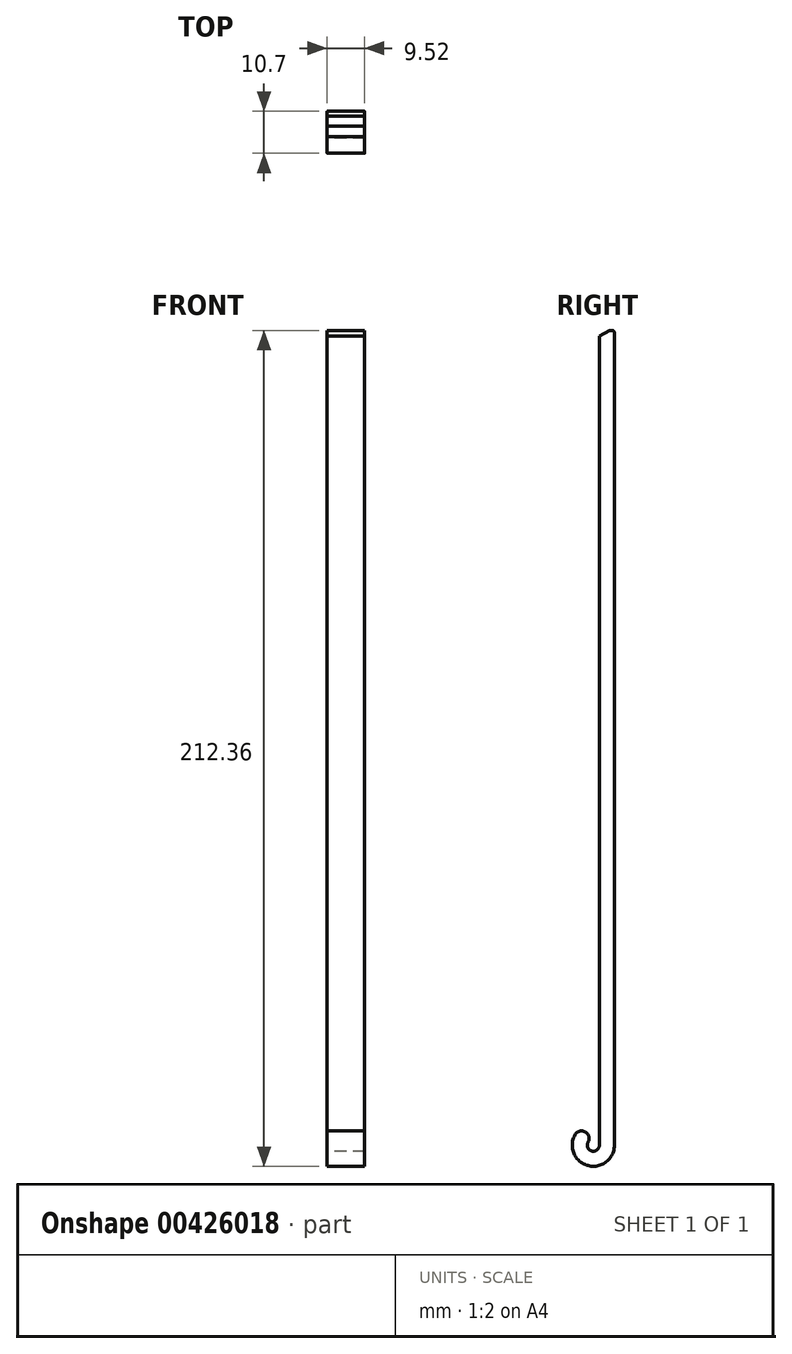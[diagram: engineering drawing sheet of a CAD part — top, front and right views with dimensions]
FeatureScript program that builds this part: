
annotation { "Feature Type Name" : "Feature", "Feature Type Description" : "" }
export const myFeature = defineFeature(function(context is Context, id is Id, definition is map)
    precondition{}
    {
        {
            var Q0;
            Q0=qCreatedBy(makeId("Front.planeOp"),FACE);
            var sketch = newSketch(context, id + "F0", { "sketchPlane" : qUnion([Q0])});
            skLineSegment(sketch, "E0", {"start": v(0, 0) * mm, "end": v(0, -176.1) * mm, "construction": true});
            skLineSegment(sketch, "E1", {"start": v(0, -176.1) * mm, "end": v(19.05, -165.1) * mm});
            skLineSegment(sketch, "E2", {"start": v(19.05, -165.1) * mm, "end": v(19.05, -57.15) * mm});
            skLineSegment(sketch, "E3", {"start": v(0, -176.1) * mm, "end": v(-19.05, -165.1) * mm});
            skLineSegment(sketch, "E4", {"start": v(-19.05, -165.1) * mm, "end": v(-19.05, -57.15) * mm});
            skCircle(sketch, "E5.cCircle", {"center": v(0, 0) * mm, "radius": 57.15 * mm, "construction": true});
            skLineSegment(sketch, "E5.0", {"start": v(-23.67, -57.15) * mm, "end": v(-57.15, -23.67) * mm});
            skLineSegment(sketch, "E5.1", {"start": v(-57.15, -23.67) * mm, "end": v(-57.15, 23.67) * mm});
            skLineSegment(sketch, "E5.2", {"start": v(-57.15, 23.67) * mm, "end": v(-23.67, 57.15) * mm});
            skLineSegment(sketch, "E5.3", {"start": v(-23.67, 57.15) * mm, "end": v(-12.7, 57.15) * mm});
            skLineSegment(sketch, "E5.4", {"start": v(23.67, 57.15) * mm, "end": v(57.15, 23.67) * mm});
            skLineSegment(sketch, "E5.5", {"start": v(57.15, 23.67) * mm, "end": v(57.15, -23.67) * mm});
            skLineSegment(sketch, "E5.6", {"start": v(57.15, -23.67) * mm, "end": v(23.67, -57.15) * mm});
            skLineSegment(sketch, "E5.7", {"start": v(23.67, -57.15) * mm, "end": v(-23.67, -57.15) * mm});
            skPoint(sketch, "E5.0.midPoint", {"position": v(-40.41, -40.41) * mm});
            skLineSegment(sketch, "E6", {"start": v(12.7, 76.2) * mm, "end": v(-12.7, 76.2) * mm});
            skCircle(sketch, "E7", {"center": v(0, 66.9) * mm, "radius": 4.76 * mm});
            skLineSegment(sketch, "E8", {"start": v(0, 66.9) * mm, "end": v(0, 0) * mm, "construction": true});
            skLineSegment(sketch, "E9", {"start": v(12.7, 76.2) * mm, "end": v(12.7, 57.15) * mm});
            skLineSegment(sketch, "E10", {"start": v(-12.7, 76.2) * mm, "end": v(-12.7, 57.15) * mm});
            skLineSegment(sketch, "E11.trimOffspring", {"start": v(12.7, 57.15) * mm, "end": v(23.67, 57.15) * mm});
            skLineSegment(sketch, "E12", {"start": v(1.59, 71.39) * mm, "end": v(1.59, 73.25) * mm});
            skLineSegment(sketch, "E13", {"start": v(-1.59, 71.39) * mm, "end": v(-1.59, 73.25) * mm});
            skArc(sketch, "E14", {"start": v(1.59, 73.25) * mm, "mid": v(0, 74.83) * mm, "end": v(-1.59, 73.25) * mm});
            skCircle(sketch, "E15", {"center": v(0, -163.4) * mm, "radius": 4.76 * mm});
            skLineSegment(sketch, "E16", {"start": v(1.59, -158.9) * mm, "end": v(1.59, -157.05) * mm});
            skLineSegment(sketch, "E17", {"start": v(-1.59, -158.9) * mm, "end": v(-1.59, -157.05) * mm});
            skArc(sketch, "E18", {"start": v(1.59, -157.05) * mm, "mid": v(0, -155.46) * mm, "end": v(-1.59, -157.05) * mm});
            skSolve(sketch);
        }
        {
            var Q0;
            Q0=qCreatedBy(makeId("Right.planeOp"),FACE);
            var sketch = newSketch(context, id + "F1", { "sketchPlane" : qUnion([Q0])});
            skLineSegment(sketch, "E19.0", {"start": v(3.18, 56.52) * mm, "end": v(34.92, 56.52) * mm});
            skLineSegment(sketch, "E19.1", {"start": v(3.17, 56.52) * mm, "end": v(3.18, 53.47) * mm});
            skLineSegment(sketch, "E19.2", {"start": v(23.93, 53.47) * mm, "end": v(3.18, 53.47) * mm});
            skLineSegment(sketch, "E19.3", {"start": v(23.93, 47.12) * mm, "end": v(23.93, 53.47) * mm});
            skLineSegment(sketch, "E19.4", {"start": v(34.92, 53.47) * mm, "end": v(23.93, 47.12) * mm});
            skLineSegment(sketch, "E19.5", {"start": v(34.92, 53.47) * mm, "end": v(34.92, 56.52) * mm});
            skSolve(sketch);
        }
        {
            var Q0;
            Q0=qCreatedBy(makeId("Right.planeOp"),FACE);
            var sketch = newSketch(context, id + "F2", { "sketchPlane" : qUnion([Q0])});
            skLineSegment(sketch, "E20", {"start": v(16.93, -149.73) * mm, "end": v(16.93, 55.81) * mm});
            skLineSegment(sketch, "E21", {"start": v(20.75, 56.77) * mm, "end": v(20.75, -149.73) * mm});
            skLineSegment(sketch, "E22", {"start": v(16.93, 55.81) * mm, "end": v(19.47, 57.28) * mm});
            skLineSegment(sketch, "E23", {"start": v(19.47, 57.28) * mm, "end": v(20.24, 57.28) * mm});
            skPoint(sketch, "E24.visualSharp", {"position": v(20.75, 57.28) * mm});
            skArc(sketch, "E24.filletArc", {"start": v(20.75, 56.77) * mm, "mid": v(20.6, 57.13) * mm, "end": v(20.24, 57.28) * mm});
            skArc(sketch, "E25", {"start": v(14.08, -148.97) * mm, "mid": v(15, -151.2) * mm, "end": v(16.93, -149.73) * mm});
            skArc(sketch, "E26", {"start": v(10.77, -147.06) * mm, "mid": v(14.02, -154.9) * mm, "end": v(20.75, -149.73) * mm});
            skLineSegment(sketch, "E27", {"start": v(15.4, -149.73) * mm, "end": v(11.67, -147.58) * mm, "construction": true});
            skLineSegment(sketch, "E28", {"start": v(15.4, -149.73) * mm, "end": v(10.18, -149.73) * mm, "construction": true});
            skArc(sketch, "E29", {"start": v(14.08, -148.97) * mm, "mid": v(13.38, -146.36) * mm, "end": v(10.77, -147.06) * mm});
            skSolve(sketch);
        }
        {
            var Q0;
            Q0=makeQuery(id+"F2.imprint","IMPRINT",FACE,{"disambiguationData":[TD([[makeQuery(id+"F2.imprint","IMPRINT",EDGE,{"derivedFrom":sQuery(id+"F2.wireOp",EDGE,"E20")}),-1.0]])]});
            extrude(context, id + "F3", {"entities" : qUnion([Q0]), "endBound" : BoundingType.SYMMETRIC, "depth" : 9.52 * mm});
        }
    });
